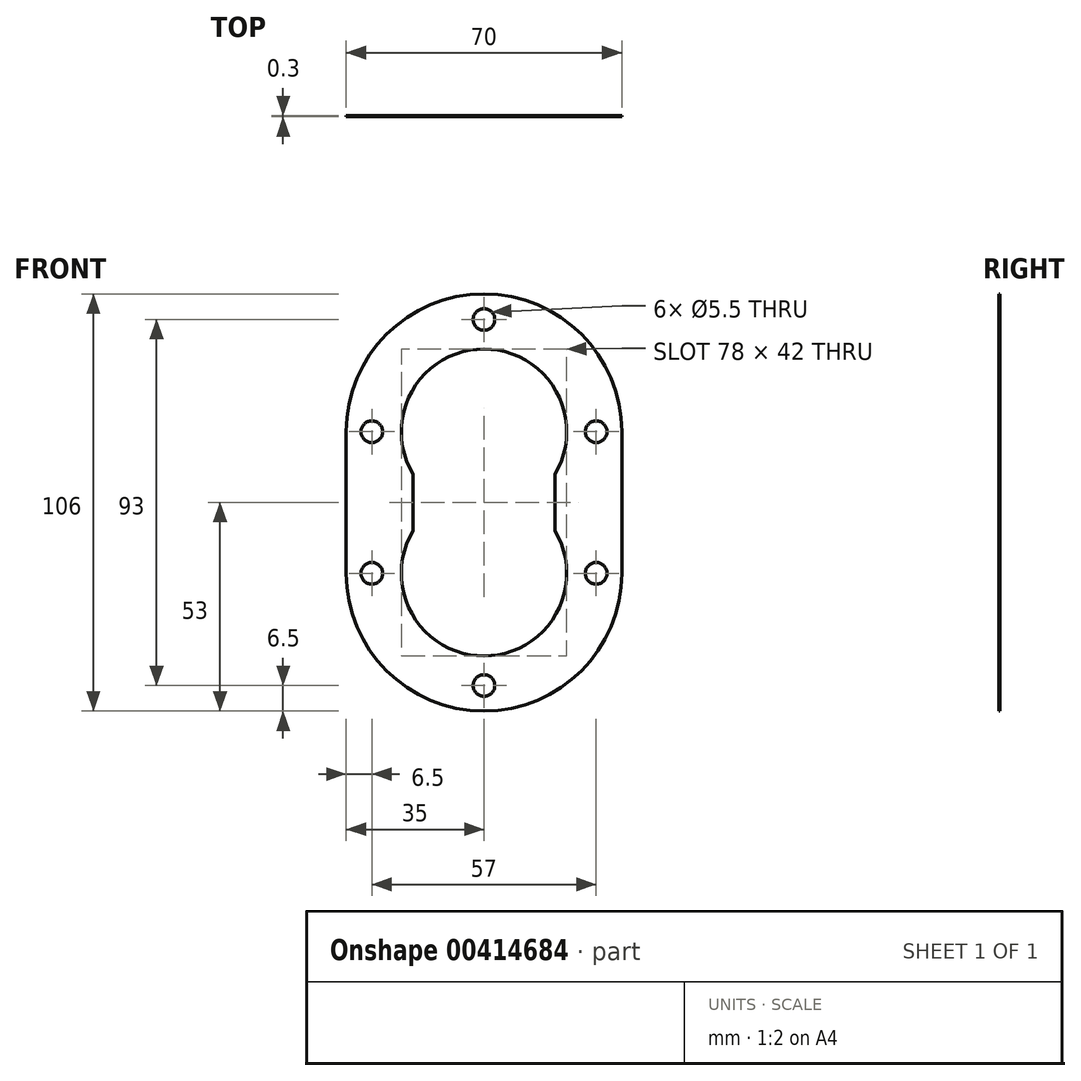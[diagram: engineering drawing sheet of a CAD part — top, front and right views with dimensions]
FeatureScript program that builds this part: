
annotation { "Feature Type Name" : "Feature", "Feature Type Description" : "" }
export const myFeature = defineFeature(function(context is Context, id is Id, definition is map)
    precondition{}
    {
        {
            var Q0;
            Q0=qCreatedBy(makeId("Front.planeOp"),FACE);
            var sketch = newSketch(context, id + "F0", { "sketchPlane" : qUnion([Q0])});
            skLineSegment(sketch, "E0", {"start": v(-18, -10.82) * mm, "end": v(-18, -25.18) * mm});
            skArc(sketch, "E1", {"start": v(18, -10.82) * mm, "mid": v(0, 21) * mm, "end": v(-18, -10.82) * mm});
            skLineSegment(sketch, "E2", {"start": v(18, -10.82) * mm, "end": v(18, -25.18) * mm});
            skArc(sketch, "E3", {"start": v(-18, -25.18) * mm, "mid": v(0, -57) * mm, "end": v(18, -25.18) * mm});
            skLineSegment(sketch, "E4", {"start": v(35, -36) * mm, "end": v(35, -25.48) * mm});
            skArc(sketch, "E5", {"start": v(35, -36) * mm, "mid": v(32.27, -49.56) * mm, "end": v(24.5, -61) * mm});
            skArc(sketch, "E6", {"start": v(24.5, -61) * mm, "mid": v(0, -71) * mm, "end": v(-24.5, -61) * mm});
            skArc(sketch, "E7", {"start": v(-24.5, -61) * mm, "mid": v(-32.27, -49.56) * mm, "end": v(-35, -36) * mm});
            skLineSegment(sketch, "E8", {"start": v(-35, -36) * mm, "end": v(-35, -25.48) * mm});
            skLineSegment(sketch, "E9", {"start": v(-35, -25.48) * mm, "end": v(-35, -18) * mm});
            skLineSegment(sketch, "E10", {"start": v(-35, -18) * mm, "end": v(-35, -10.52) * mm});
            skLineSegment(sketch, "E11", {"start": v(-35, -10.52) * mm, "end": v(-35, 0) * mm});
            skArc(sketch, "E12", {"start": v(-35, 0) * mm, "mid": v(0, 35) * mm, "end": v(35, 0) * mm});
            skLineSegment(sketch, "E13", {"start": v(35, -10.52) * mm, "end": v(35, 0) * mm});
            skLineSegment(sketch, "E14", {"start": v(35, -18) * mm, "end": v(35, -10.52) * mm});
            skLineSegment(sketch, "E15", {"start": v(35, -25.48) * mm, "end": v(35, -18) * mm});
            skSolve(sketch);
        }
        {
            var Q0;
            Q0 = qSketchRegion(id + "F0", true);
            extrude(context, id + "F1", {"entities" : qUnion([Q0]), "depth" : 0.3 * mm});
        }
        {
            var Q0;
            Q0=makeQuery(id+"F1.opExtrude","CAP_FACE",FACE,{"disambiguationData":[OSD([sQuery(id+"F0.wireOp",EDGE,"E0"),sQuery(id+"F0.wireOp",EDGE,"E1"),sQuery(id+"F0.wireOp",EDGE,"E2"),sQuery(id+"F0.wireOp",EDGE,"E3"),sQuery(id+"F0.wireOp",EDGE,"E4"),sQuery(id+"F0.wireOp",EDGE,"E5"),sQuery(id+"F0.wireOp",EDGE,"E6"),sQuery(id+"F0.wireOp",EDGE,"E7"),sQuery(id+"F0.wireOp",EDGE,"E8"),sQuery(id+"F0.wireOp",EDGE,"E9"),sQuery(id+"F0.wireOp",EDGE,"E10"),sQuery(id+"F0.wireOp",EDGE,"E11"),sQuery(id+"F0.wireOp",EDGE,"E12"),sQuery(id+"F0.wireOp",EDGE,"E13"),sQuery(id+"F0.wireOp",EDGE,"E14"),sQuery(id+"F0.wireOp",EDGE,"E15")])],"isStart":false});
            var sketch = newSketch(context, id + "F2", { "sketchPlane" : qUnion([Q0])});
            skArc(sketch, "E16.0", {"start": v(-35, 0) * mm, "mid": v(0, 35) * mm, "end": v(35, 0) * mm});
            skLineSegment(sketch, "E17.0", {"start": v(35, -36) * mm, "end": v(35, 0) * mm});
            skArc(sketch, "E18.0", {"start": v(35, -36) * mm, "mid": v(0, -71) * mm, "end": v(-35, -36) * mm});
            skLineSegment(sketch, "E19.0", {"start": v(-35, -36) * mm, "end": v(-35, 0) * mm});
            skArc(sketch, "E20.0", {"start": v(-28.5, 0) * mm, "mid": v(0, 28.5) * mm, "end": v(28.5, 0) * mm});
            skLineSegment(sketch, "E20.1", {"start": v(-28.5, -36) * mm, "end": v(-28.5, 0) * mm});
            skArc(sketch, "E20.2", {"start": v(28.5, -36) * mm, "mid": v(0, -64.5) * mm, "end": v(-28.5, -36) * mm});
            skLineSegment(sketch, "E20.3", {"start": v(28.5, -36) * mm, "end": v(28.5, 0) * mm});
            skPoint(sketch, "E21", {"position": v(0, 28.5) * mm});
            skPoint(sketch, "E22", {"position": v(-28.5, 0) * mm});
            skPoint(sketch, "E23", {"position": v(28.5, 0) * mm});
            skPoint(sketch, "E24", {"position": v(28.5, -36) * mm});
            skPoint(sketch, "E25", {"position": v(0, -64.5) * mm});
            skPoint(sketch, "E26", {"position": v(-28.5, -36) * mm});
            skSolve(sketch);
        }
        {
            var Q0;
            Q0=sQuery(id+"F2.wireOp",VERTEX,"E21");
            var Q1;
            Q1=sQuery(id+"F2.wireOp",VERTEX,"E22");
            var Q2;
            Q2=sQuery(id+"F2.wireOp",VERTEX,"E26");
            var Q3;
            Q3=sQuery(id+"F2.wireOp",VERTEX,"E25");
            var Q4;
            Q4=sQuery(id+"F2.wireOp",VERTEX,"E24");
            var Q5;
            Q5=sQuery(id+"F2.wireOp",VERTEX,"E23");
            var Q6;
            Q6=makeQuery(id+"F1.opExtrude","SWEPT_BODY",BODY,{"disambiguationData":[OSD([sQuery(id+"F0.wireOp",EDGE,"E0"),sQuery(id+"F0.wireOp",EDGE,"E1"),sQuery(id+"F0.wireOp",EDGE,"E2"),sQuery(id+"F0.wireOp",EDGE,"E3"),sQuery(id+"F0.wireOp",EDGE,"E4"),sQuery(id+"F0.wireOp",EDGE,"E5"),sQuery(id+"F0.wireOp",EDGE,"E6"),sQuery(id+"F0.wireOp",EDGE,"E7"),sQuery(id+"F0.wireOp",EDGE,"E8"),sQuery(id+"F0.wireOp",EDGE,"E9"),sQuery(id+"F0.wireOp",EDGE,"E10"),sQuery(id+"F0.wireOp",EDGE,"E11"),sQuery(id+"F0.wireOp",EDGE,"E12"),sQuery(id+"F0.wireOp",EDGE,"E13"),sQuery(id+"F0.wireOp",EDGE,"E14"),sQuery(id+"F0.wireOp",EDGE,"E15")])]});
            hole(context, id + "F3", {"style" : HoleStyle.SIMPLE, "endStyle" : HoleEndStyle.THROUGH, "holeDiameter" : 5.5 * mm, "isTappedThrough" : true, "tappedDepth" : 12 * mm, "tapClearance" : 3, "startFromSketch" : true, "locations" : qUnion([Q0, Q1, Q2, Q3, Q4, Q5]), "scope" : qUnion([Q6])});
        }
    });
